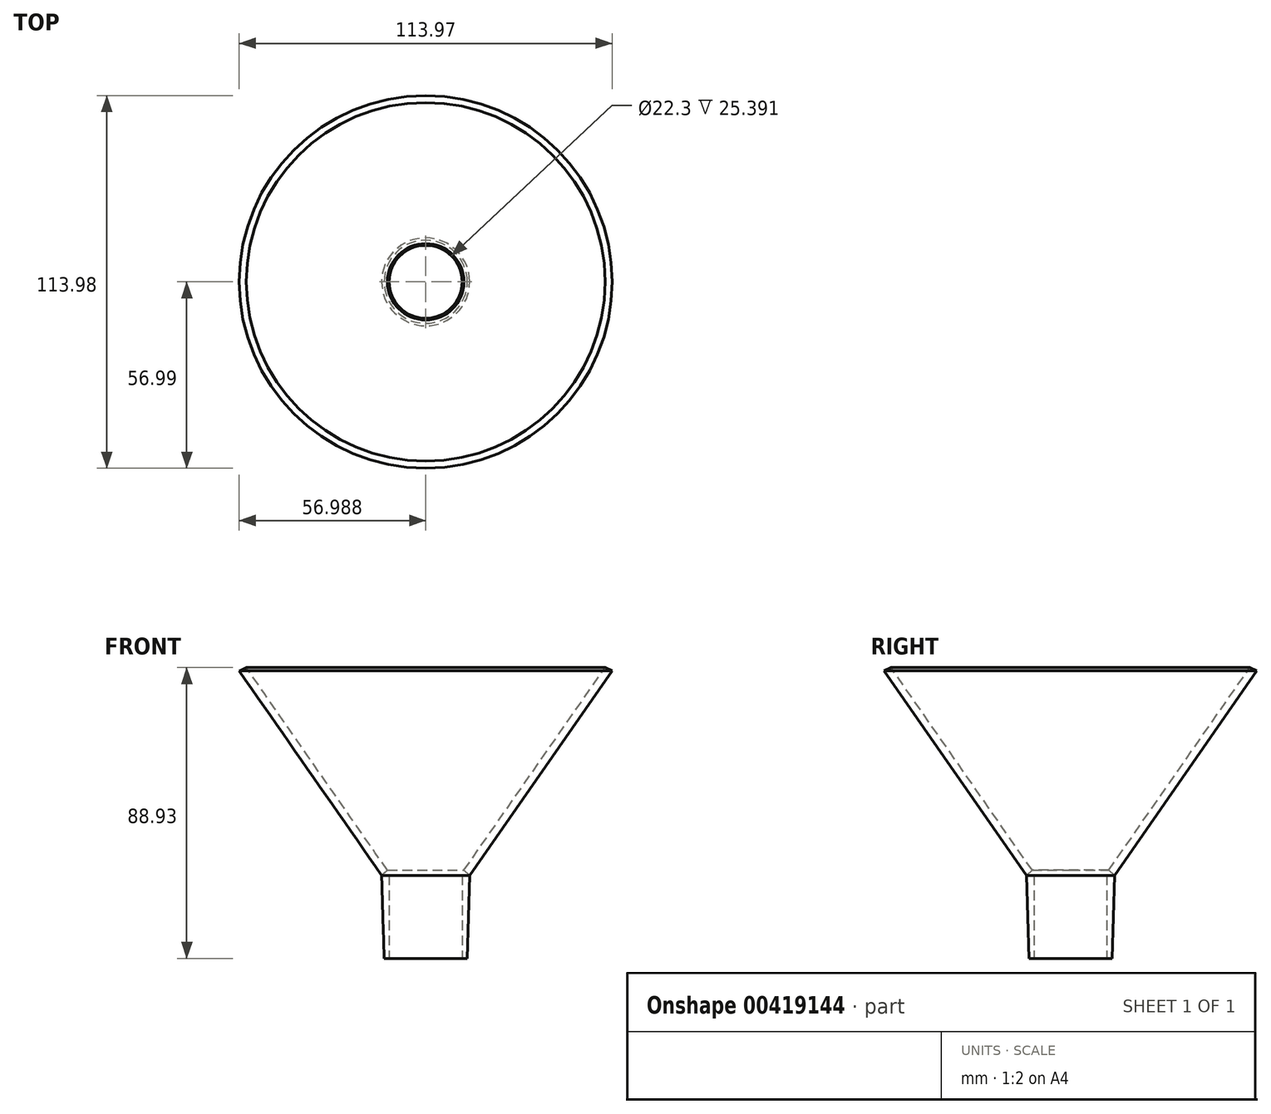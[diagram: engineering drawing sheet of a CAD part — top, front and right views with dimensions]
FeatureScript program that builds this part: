
annotation { "Feature Type Name" : "Feature", "Feature Type Description" : "" }
export const myFeature = defineFeature(function(context is Context, id is Id, definition is map)
    precondition{}
    {
        {
            var Q0;
            Q0=qCreatedBy(makeId("Front.planeOp"),FACE);
            var sketch = newSketch(context, id + "F0", { "sketchPlane" : qUnion([Q0])});
            skLineSegment(sketch, "E0", {"start": v(-13.45, -29.7) * mm, "end": v(-0.75, -29.7) * mm});
            skLineSegment(sketch, "E1", {"start": v(-0.75, -29.7) * mm, "end": v(0, -4.3) * mm});
            skLineSegment(sketch, "E2", {"start": v(0, -4.3) * mm, "end": v(43.53, 58.24) * mm});
            skLineSegment(sketch, "E3", {"start": v(43.53, 58.24) * mm, "end": v(0, -4.3) * mm});
            skLineSegment(sketch, "E4", {"start": v(-1.76, -2.74) * mm, "end": v(41.38, 59.24) * mm});
            skLineSegment(sketch, "E5", {"start": v(41.38, 59.24) * mm, "end": v(43.53, 58.24) * mm});
            skLineSegment(sketch, "E6", {"start": v(-13.45, -29.7) * mm, "end": v(-13.45, -4.3) * mm});
            skLineSegment(sketch, "E7", {"start": v(-13.45, -4.3) * mm, "end": v(0, -4.3) * mm});
            skLineSegment(sketch, "E8", {"start": v(-1.76, -2.74) * mm, "end": v(0, -4.3) * mm});
            skSolve(sketch);
        }
        {
            var Q0;
            Q0 = qSketchRegion(id + "F0", true);
            var Q1;
            Q1=sQuery(id+"F0.wireOp",EDGE,"E6");
            revolve(context, id + "F1", {"entities" : qUnion([Q0]), "axis" : qUnion([Q1]), "revolveType" : RevolveType.FULL});
        }
        {
            var Q0;
            Q0=makeQuery(id+"F1.opRevolve","SWEPT_FACE",FACE,{"disambiguationData":[OSD([sQuery(id+"F0.wireOp",EDGE,"E0")])]});
            var sketch = newSketch(context, id + "F2", { "sketchPlane" : qUnion([Q0])});
            skCircle(sketch, "E9", {"center": v(-13.45, 0) * mm, "radius": 11.15 * mm});
            skSolve(sketch);
        }
        {
            var Q0;
            Q0=makeQuery(id+"F2.imprint","IMPRINT",FACE,{"disambiguationData":[TD([[makeQuery(id+"F2.imprint","IMPRINT",EDGE,{"derivedFrom":sQuery(id+"F2.wireOp",EDGE,"E9")}),1.0]])]});
            extrude(context, id + "F3", {"entities" : qUnion([Q0]), "operationType" : NewBodyOperationType.REMOVE, "oppositeDirection" : true, "depth" : 25.4 * mm});
        }
    });
